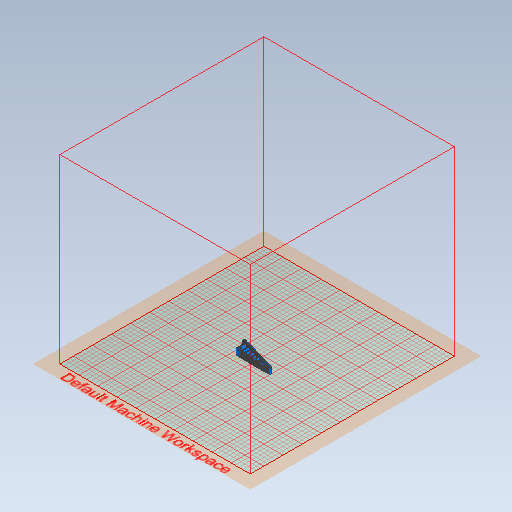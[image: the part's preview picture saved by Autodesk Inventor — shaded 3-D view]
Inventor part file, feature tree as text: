
AUTODESK INVENTOR PART (.ipt)
format: ipt  version: 2021 (Build 250183000, 183)  size: 1,063,424 bytes
history: native  units: mm
features: extrude x3, sketch x3, other x1, fillet x1
ambient origin geometry x8: Origin, YZ Plane, XZ Plane, XY Plane, X Axis, Y Axis, Z Axis, Center Point
bodies: Body1 (feature_tree)
feature tree (8):
  other  "Sólido1"
  extrude  "Extrusão1"  Depth=2.0mm
  extrude  "Extrusão2"  Depth=2.0mm
  extrude  "Extrusão3"  TaperAngle=45.0deg  [1 undecoded]
  fillet  "Arredondamento1"  Radius=7.5mm
  sketch  "Esboço1"  dims[d4=2.5mm d6=2.0mm]
  sketch  "Esboço2"  dims[d39=0.8mm d40=2.0mm]
  sketch  "Esboço3"  dims[d41=2.0mm d44=45.0deg d46=0.8mm d47=2.0mm d48=2.0mm d49=45.0deg d53=7.5mm d54=0.8mm d55=2.0mm d56=2.0mm d57=45.0deg d58=3.0mm d59=2.5mm d60=45.0deg d63=0.8mm d64=2.0mm d65=2.0mm d66=45.0deg d67=3.0mm d68=2.5mm d69=45.0deg d72=0.8mm d73=2.0mm d74=2.0mm d75=45.0deg d76=3.0mm d77=2.5mm d78=45.0deg d81=0.8mm d82=2.0mm d83=2.0mm d84=45.0deg d85=3.0mm d86=2.5mm d87=45.0deg d117=7.5mm d119=7.5mm d120=7.5mm d124=7.5mm d125=0.8mm d126=2.0mm d127=2.0mm d128=45.0deg d129=0.8mm d130=2.0mm d131=2.5mm d132=45.0deg d155=7.5mm d157=0.8mm d158=2.0mm d159=2.0mm d160=45.0deg d161=0.8mm d162=2.0mm d163=2.0mm d164=45.0deg d167=7.5mm d168=0.8mm d169=0.8mm d170=7.5mm d171=7.5mm d178=12.0mm d179=0.0mm d181=3.0mm d182=1.5mm d183=5.0mm d184=1.5mm d189=5.0mm d191=2.0mm d194=2.792527mm d203=6.0mm d207=0.8mm d208=60.0deg d209=6.4mm d217=0.1mm d218=10.0mm d219=0.0mm d220=5.0mm d221=1.5mm d222=70.0mm d223=20.0mm d224=8.0mm d225=7.0mm d227=2.0mm d228=260.0mm d230=2.5mm d231=10.0mm d233=10.0mm d235=2.0mm d237=1.5mm d238=5.0mm d239=5.0mm d240=0.2mm d241=0.0mm d242=0.5mm]
note: 1 required parameter value undecoded (feature->parameter linkage not recoverable at this tier; creation-order binding heuristic only, values carry confidence <= 0.55)
